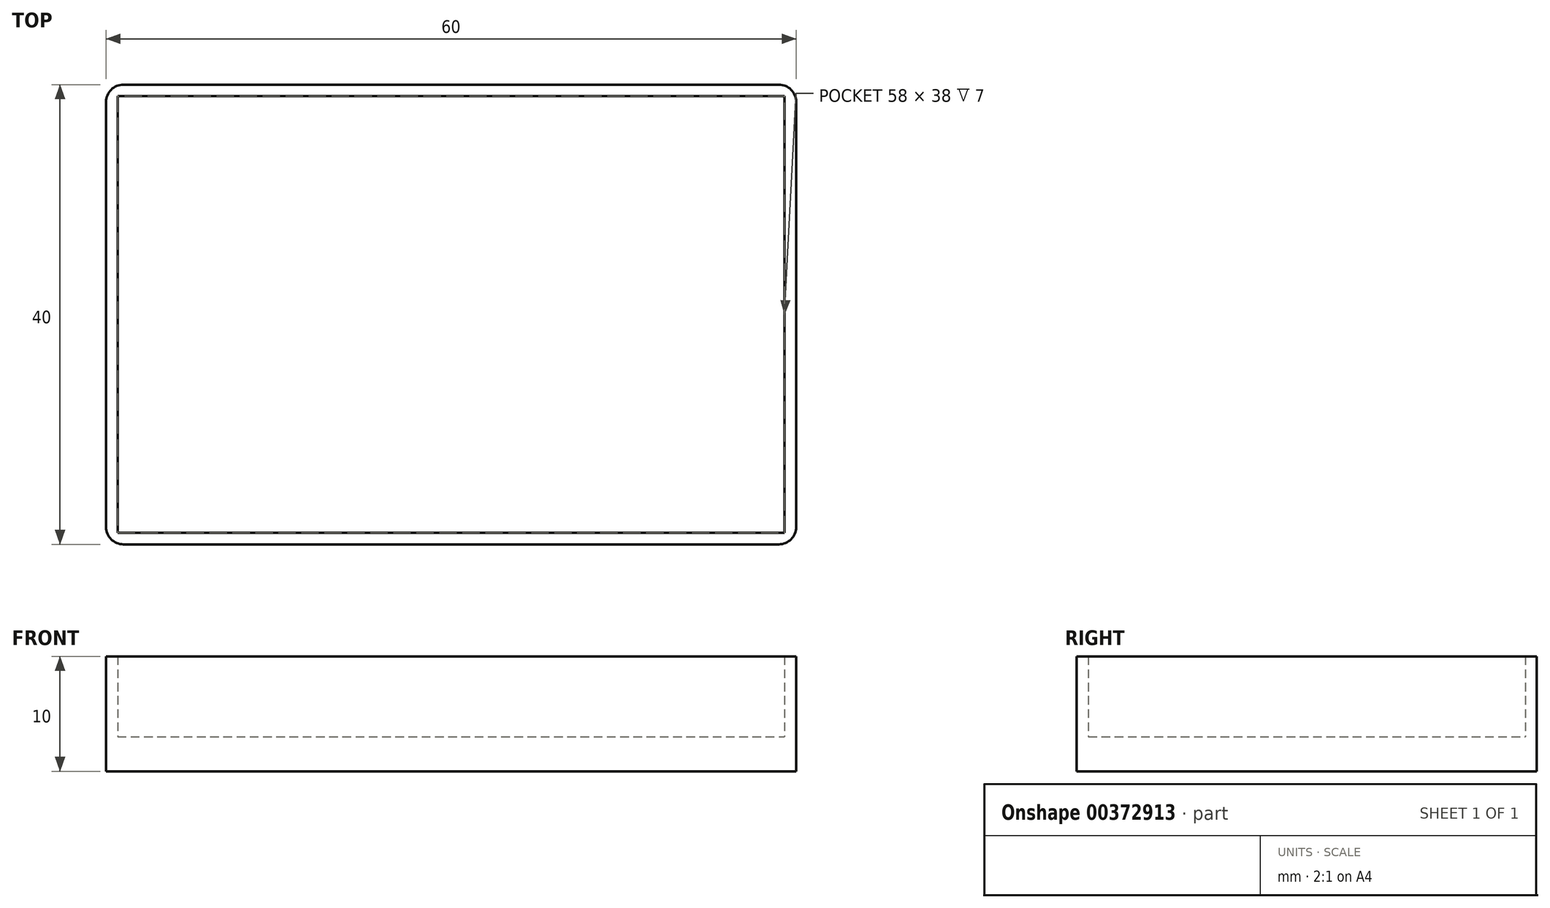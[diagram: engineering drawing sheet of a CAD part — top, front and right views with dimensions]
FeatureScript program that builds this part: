
annotation { "Feature Type Name" : "Feature", "Feature Type Description" : "" }
export const myFeature = defineFeature(function(context is Context, id is Id, definition is map)
    precondition{}
    {
        {
            var Q0;
            Q0=qCreatedBy(makeId("Top.planeOp"),FACE);
            var sketch = newSketch(context, id + "F0", { "sketchPlane" : qUnion([Q0])});
            skLineSegment(sketch, "E0.bottom", {"start": v(-30, -20) * mm, "end": v(30, -20) * mm});
            skLineSegment(sketch, "E0.top", {"start": v(-30, 20) * mm, "end": v(30, 20) * mm});
            skLineSegment(sketch, "E0.left", {"start": v(-30, -20) * mm, "end": v(-30, 20) * mm});
            skLineSegment(sketch, "E0.right", {"start": v(30, -20) * mm, "end": v(30, 20) * mm});
            skLineSegment(sketch, "E1.bottom", {"start": v(-29, -19) * mm, "end": v(29, -19) * mm});
            skLineSegment(sketch, "E1.top", {"start": v(-29, 19) * mm, "end": v(29, 19) * mm});
            skLineSegment(sketch, "E1.left", {"start": v(-29, -19) * mm, "end": v(-29, 19) * mm});
            skLineSegment(sketch, "E1.right", {"start": v(29, -19) * mm, "end": v(29, 19) * mm});
            skSolve(sketch);
        }
        {
            var Q0;
            Q0=makeQuery(id+"F0.imprint","IMPRINT",FACE,{"disambiguationData":[TD([[makeQuery(id+"F0.imprint","IMPRINT",EDGE,{"derivedFrom":sQuery(id+"F0.wireOp",EDGE,"E1.bottom")}),1.0]])]});
            extrude(context, id + "F1", {"entities" : qUnion([Q0]), "depth" : 3 * mm});
        }
        {
            var Q0;
            Q0=makeQuery(id+"F0.imprint","IMPRINT",FACE,{"disambiguationData":[TD([[makeQuery(id+"F0.imprint","IMPRINT",EDGE,{"derivedFrom":sQuery(id+"F0.wireOp",EDGE,"E0.bottom")}),1.0]])]});
            extrude(context, id + "F2", {"entities" : qUnion([Q0]), "operationType" : NewBodyOperationType.ADD, "depth" : 10 * mm});
        }
        {
            var Q0;
            Q0=makeQuery(id+"F2.opExtrude","SWEPT_EDGE",EDGE,{"disambiguationData":[OSD([sQuery(id+"F0.wireOp",EDGE,"E0.bottom"),sQuery(id+"F0.wireOp",EDGE,"E0.left")])]});
            var Q1;
            Q1=makeQuery(id+"F2.opExtrude","SWEPT_EDGE",EDGE,{"disambiguationData":[OSD([sQuery(id+"F0.wireOp",EDGE,"E0.bottom"),sQuery(id+"F0.wireOp",EDGE,"E0.right")])]});
            var Q2;
            Q2=makeQuery(id+"F2.opExtrude","SWEPT_EDGE",EDGE,{"disambiguationData":[OSD([sQuery(id+"F0.wireOp",EDGE,"E0.top"),sQuery(id+"F0.wireOp",EDGE,"E0.right")])]});
            var Q3;
            Q3=makeQuery(id+"F2.opExtrude","SWEPT_EDGE",EDGE,{"disambiguationData":[OSD([sQuery(id+"F0.wireOp",EDGE,"E0.top"),sQuery(id+"F0.wireOp",EDGE,"E0.left")])]});
            fillet(context, id + "F3", {"entities" : qUnion([Q0, Q1, Q2, Q3]), "radius" : 1.5 * mm, "tangentPropagation" : true, "allowEdgeOverflow" : false});
        }
    });
